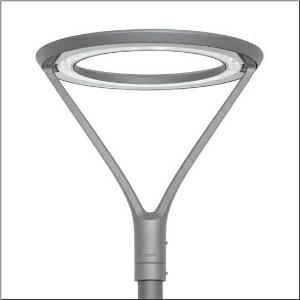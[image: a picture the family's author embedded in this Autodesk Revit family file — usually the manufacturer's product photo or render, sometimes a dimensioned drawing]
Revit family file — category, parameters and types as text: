
# Revit family: dl_r__20_led___pl1_2s_5xa51283ws008p_d70c
name_source: partatom
category: Lighting Fixtures
units: mm (PartAtom-declared; Revit-internal decimal feet)

## family parameters
Cut with Voids When Loaded = No
Host = Face
Light Source = No
Part Type = Normal
Room Calculation Point = No
Round Connector Dimension = Use Diameter
Shared = No

## types (1)
- --- (1 x LED 3000K / CRI = 80 (unbekannt), 4210 lm, 3000K)
    Apparent Load = 53 VA
    CIE Flux Codes = 34 78 98 100 100
    Color Rendering = 80
    Color Temperature = 3000K
    Default Elevation = 1800 mm
    Description = DL® 20 LED, mast luminaire, primary light control with reflector, highly specular, primary optical cover: cover, of toughened safety glass of clear glass with excellent transmission level, light distribution: PL1.2s, light emission: direct distribution, primary light characteristic: symmetric, installation type: post-top, LED High Power LED, rated luminous flux: 4.210 lm, light colour: 830, colour temperature: 3000K, control gear: ECG Plus, control: overheat protection, power reduction, digital communication interface, constant luminous flux control, time-dependent luminous flux control, flexible luminous flux parameterisation, electronic power reduction, mains connection: 220..240V, 50/60Hz, connection cable pre-assembled, cable length: 5 m, start of lifetime: 53 W, end of lifetime: 54 W, reduction: 24 W, luminaire housing, upper part, of cast aluminium, powder-coated, Siteco® metallic grey (DB 702S), diameter: 690 mm, height: 690mm, spigot size: 76mm (post-top), luminaire housing, of cast aluminium, powder-coated, Siteco® metallic grey (DB 702S), protection rating (complete): IP66, insulation class (complete): insulation class II (safety insulation), certification: CE, ENEC, VDE, impact resistance: IK08, permissible ambient temperature for indoor applications: -25..+30°C, standard-compliant lighting for roads and squares, packaging unit: 1 piece

Light Distribution: PL1.2s
    Height = 690 mm
    Lamp = 1 x LED 3000K / CRI >= 80 (unbekannt)
    Lamp Light Flux = 4210 lm
    Lamp count = 1
    Length = 690 mm
    Luminous efficacy = 80 lm/W
    Manufacturer = Siteco
    ModVariant = No
    Model = 5XA51283WS008P
    Number of Poles = 1
    OnlyDefault = Yes
    Power Factor = 1
    Product Name = DL® 20 LED | PL1.2s
    Product group = mast luminaire | pylon top
    ProductGroupID = 6100
    Protection Class = Protection class II
    Protection Degree = IP 66
    RLX_Detail_Level = 1
    RlxData = <blob elided: 204425 chars, md5=47ddb162>
    Socket = socket
    Standby Power = 0 W
    System Light Flux = 4210 lm
    System Power = 53 W
    Type Comments = factory setting: luminous flux: 100 % | dim-lin: 254 | 683 mA
    Type Image = l_1006001.jpg
    URL = http://relux.com
    VarID = @adj_141491
    Voltage = 0 V
    Weight = 0.00 kg
    Width = 0 mm  [stored 0 ft]

note: [stored X ft] marks values corroborated as IEEE doubles in the binary element streams (Revit-internal decimal feet)

## geometry (parser evidence)
native form markers: Blend x4, Sweep x10
no freeform markers — native parametric forms only
